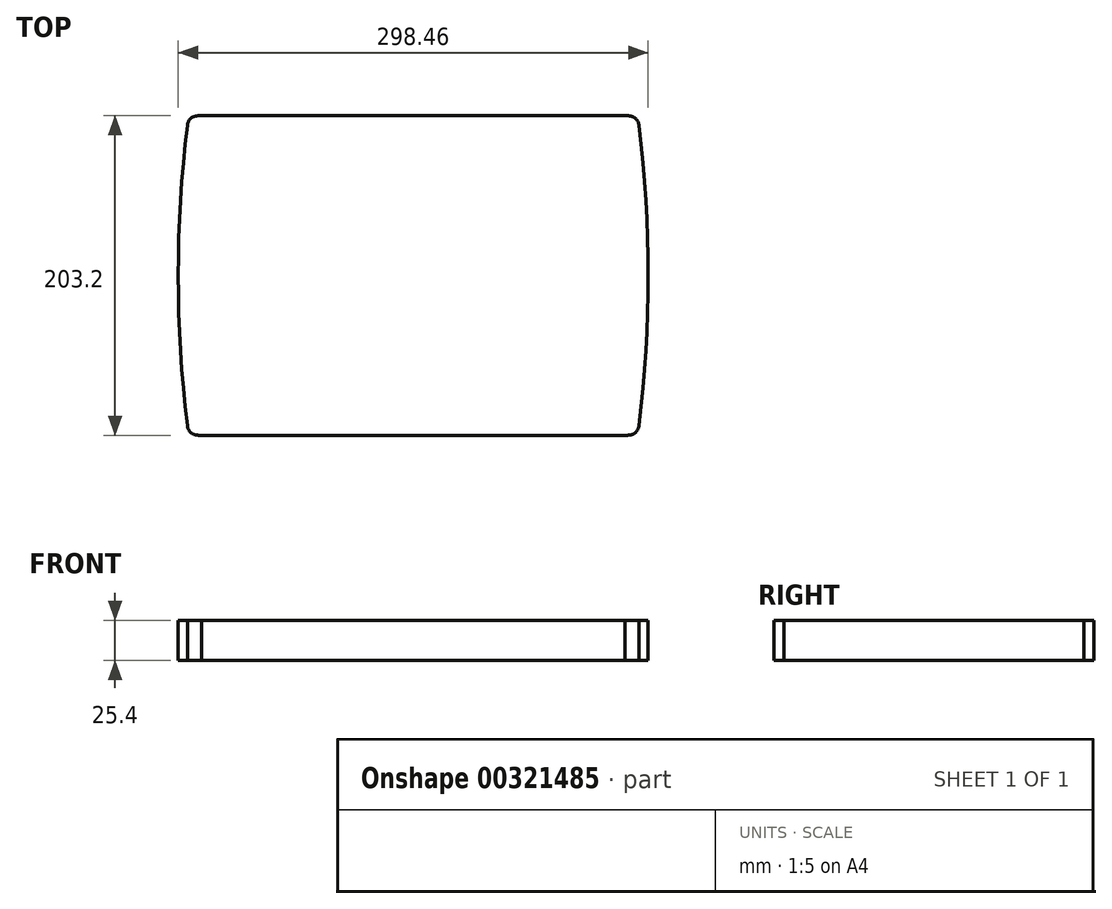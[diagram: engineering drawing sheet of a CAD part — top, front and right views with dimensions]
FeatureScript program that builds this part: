
annotation { "Feature Type Name" : "Feature", "Feature Type Description" : "" }
export const myFeature = defineFeature(function(context is Context, id is Id, definition is map)
    precondition{}
    {
        {
            var Q0;
            Q0=qCreatedBy(makeId("Top.planeOp"),FACE);
            var sketch = newSketch(context, id + "F0", { "sketchPlane" : qUnion([Q0])});
            skLineSegment(sketch, "E0.bottom", {"start": v(-134.46, 101.6) * mm, "end": v(0, 101.6) * mm});
            skPoint(sketch, "E0.middle", {"position": v(0, 0) * mm});
            skLineSegment(sketch, "E1", {"start": v(0, 0) * mm, "end": v(0, 116.26) * mm, "construction": true});
            skLineSegment(sketch, "E2", {"start": v(0, 0) * mm, "end": v(-174.22, 0) * mm, "construction": true});
            skArc(sketch, "E3", {"start": v(-143.41, 95.25) * mm, "mid": v(-147.77, 47.71) * mm, "end": v(-149.23, 0) * mm});
            skFitSpline(sketch, "E4", {"points": [v(-143.41, 95.25) * mm, v(-134.46, 101.6) * mm], "startDerivative": vector(2.47, 16.03) * mm, "endDerivative": vector(14.38, 0.27) * mm});
            skFitSpline(sketch, "E5.MirrorCS", {"points": [v(-143.41, -95.25) * mm, v(-134.46, -101.6) * mm], "startDerivative": vector(2.47, -16.03) * mm, "endDerivative": vector(14.38, -0.27) * mm});
            skArc(sketch, "E6.MirrorCS", {"start": v(-143.41, -95.25) * mm, "mid": v(-147.77, -47.71) * mm, "end": v(-149.23, 0) * mm});
            skLineSegment(sketch, "E7.MirrorCS", {"start": v(-134.46, -101.6) * mm, "end": v(0, -101.6) * mm});
            skLineSegment(sketch, "E8.MirrorCS", {"start": v(134.46, -101.6) * mm, "end": v(0, -101.6) * mm});
            skLineSegment(sketch, "E9.MirrorCS", {"start": v(134.46, 101.6) * mm, "end": v(0, 101.6) * mm});
            skFitSpline(sketch, "E10.MirrorCS", {"points": [v(143.41, -95.25) * mm, v(134.46, -101.6) * mm], "startDerivative": vector(-2.47, -16.03) * mm, "endDerivative": vector(-14.38, -0.27) * mm});
            skFitSpline(sketch, "E11.MirrorCS", {"points": [v(143.41, 95.25) * mm, v(134.46, 101.6) * mm], "startDerivative": vector(-2.47, 16.03) * mm, "endDerivative": vector(-14.38, 0.27) * mm});
            skArc(sketch, "E12.MirrorCS", {"start": v(143.41, -95.25) * mm, "mid": v(147.77, -47.71) * mm, "end": v(149.23, 0) * mm});
            skArc(sketch, "E13.MirrorCS", {"start": v(143.41, 95.25) * mm, "mid": v(147.77, 47.71) * mm, "end": v(149.23, 0) * mm});
            skSolve(sketch);
        }
        {
            var Q0;
            Q0 = qSketchRegion(id + "F0", true);
            extrude(context, id + "F1", {"entities" : qUnion([Q0]), "depth" : 25.4 * mm});
        }
    });
